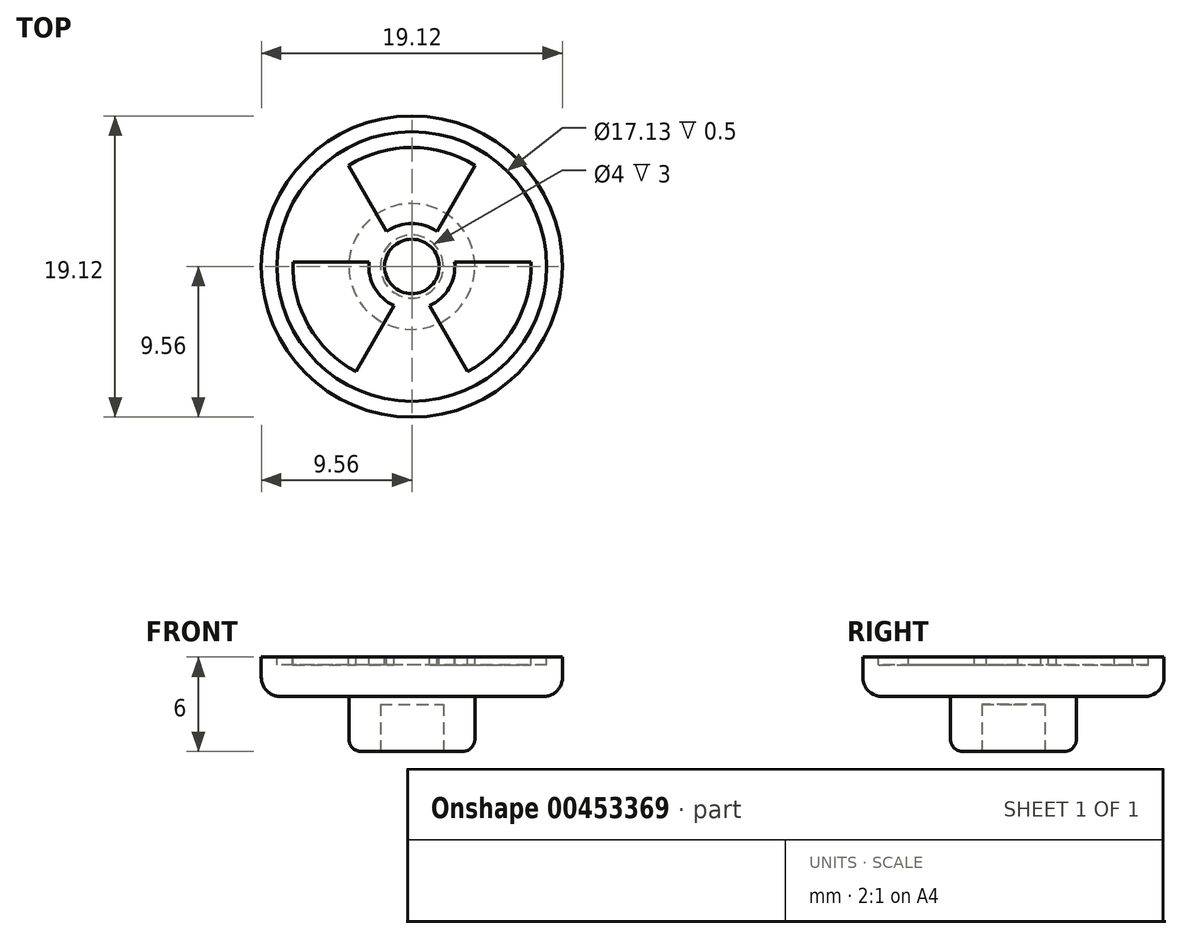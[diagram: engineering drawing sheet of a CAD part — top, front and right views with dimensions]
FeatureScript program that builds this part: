
annotation { "Feature Type Name" : "Feature", "Feature Type Description" : "" }
export const myFeature = defineFeature(function(context is Context, id is Id, definition is map)
    precondition{}
    {
        {
            var Q0;
            Q0=qCreatedBy(makeId("Top.planeOp"),FACE);
            var sketch = newSketch(context, id + "F0", { "sketchPlane" : qUnion([Q0])});
            skCircle(sketch, "E0", {"center": v(0, 0) * mm, "radius": 9.56 * mm});
            skSolve(sketch);
        }
        {
            var Q0;
            Q0=makeQuery(id+"F0.imprint","IMPRINT",FACE,{"disambiguationData":[TD([[makeQuery(id+"F0.imprint","IMPRINT",EDGE,{"derivedFrom":sQuery(id+"F0.wireOp",EDGE,"E0")}),1.0]])]});
            extrude(context, id + "F1", {"entities" : qUnion([Q0]), "depth" : 2.5 * mm, "offsetDistance" : 25 * mm});
        }
        {
            var Q0;
            Q0=makeQuery(id+"F1.opExtrude","CAP_FACE",FACE,{"disambiguationData":[OSD([sQuery(id+"F0.wireOp",EDGE,"E0")])],"isStart":false});
            var sketch = newSketch(context, id + "F2", { "sketchPlane" : qUnion([Q0])});
            skCircle(sketch, "E1", {"center": v(0, 0) * mm, "radius": 1.73 * mm});
            skArc(sketch, "E2", {"start": v(1.6, 2.22) * mm, "mid": v(0, 2.73) * mm, "end": v(-1.6, 2.22) * mm});
            skLineSegment(sketch, "E3", {"start": v(-1.6, 2.22) * mm, "end": v(-4.52, 7.28) * mm});
            skLineSegment(sketch, "E4", {"start": v(1.6, 2.22) * mm, "end": v(4.52, 7.28) * mm});
            skArc(sketch, "E5", {"start": v(4.52, 7.28) * mm, "mid": v(0, 8.56) * mm, "end": v(-4.52, 7.28) * mm});
            skLineSegment(sketch, "E6", {"start": v(0, 0) * mm, "end": v(8.28, 4.78) * mm, "construction": true});
            skLineSegment(sketch, "E7", {"start": v(0, 0) * mm, "end": v(-8.28, 4.78) * mm, "construction": true});
            skLineSegment(sketch, "E8", {"start": v(0, 0) * mm, "end": v(0, -15.72) * mm, "construction": true});
            skLineSegment(sketch, "E9.MirrorCS", {"start": v(2.72, 0.27) * mm, "end": v(8.56, 0.27) * mm});
            skArc(sketch, "E10.MirrorCS", {"start": v(2.72, 0.27) * mm, "mid": v(2.36, -1.36) * mm, "end": v(1.12, -2.49) * mm});
            skLineSegment(sketch, "E11.MirrorCS", {"start": v(1.12, -2.49) * mm, "end": v(4.04, -7.55) * mm});
            skArc(sketch, "E12.MirrorCS", {"start": v(8.56, 0.27) * mm, "mid": v(7.42, -4.28) * mm, "end": v(4.04, -7.55) * mm});
            skLineSegment(sketch, "E13.MirrorCS", {"start": v(-2.72, 0.27) * mm, "end": v(-8.56, 0.27) * mm});
            skArc(sketch, "E14.MirrorCS", {"start": v(-1.12, -2.49) * mm, "mid": v(-2.36, -1.36) * mm, "end": v(-2.72, 0.27) * mm});
            skLineSegment(sketch, "E15.MirrorCS", {"start": v(-1.12, -2.49) * mm, "end": v(-4.04, -7.55) * mm});
            skArc(sketch, "E16.MirrorCS", {"start": v(-4.04, -7.55) * mm, "mid": v(-7.42, -4.28) * mm, "end": v(-8.56, 0.27) * mm});
            skCircle(sketch, "E17", {"center": v(0, 0) * mm, "radius": 8.56 * mm});
            skCircle(sketch, "E18", {"center": v(0, 0) * mm, "radius": 7.56 * mm});
            skSolve(sketch);
        }
        {
            var Q0;
            Q0 = qSketchRegion(id + "F2", true);
            var Q1;
            Q1=makeQuery(id+"F2.imprint","IMPRINT",FACE,{"disambiguationData":[TD([[makeQuery(id+"F2.imprint","IMPRINT",EDGE,{"derivedFrom":sQuery(id+"F2.wireOp",EDGE,"E1")}),-1.0]])]});
            extrude(context, id + "F3", {"entities" : qUnion([Q0, Q1]), "operationType" : NewBodyOperationType.REMOVE, "oppositeDirection" : true, "depth" : .5 * mm, "offsetDistance" : 25 * mm});
        }
        {
            var Q0;
            Q0=makeQuery(id+"F1.opExtrude","CAP_FACE",FACE,{"disambiguationData":[OSD([sQuery(id+"F0.wireOp",EDGE,"E0")])],"isStart":true});
            var sketch = newSketch(context, id + "F4", { "sketchPlane" : qUnion([Q0])});
            skCircle(sketch, "E19", {"center": v(0, 0) * mm, "radius": 4 * mm});
            skSolve(sketch);
        }
        {
            var Q0;
            Q0=makeQuery(id+"F4.imprint","IMPRINT",FACE,{"disambiguationData":[TD([[makeQuery(id+"F4.imprint","IMPRINT",EDGE,{"derivedFrom":sQuery(id+"F4.wireOp",EDGE,"E19")}),1.0]])]});
            extrude(context, id + "F5", {"entities" : qUnion([Q0]), "operationType" : NewBodyOperationType.ADD, "depth" : 3.5 * mm, "offsetDistance" : 25 * mm});
        }
        {
            var Q0;
            Q0=makeQuery(id+"F1.opExtrude","CAP_EDGE",EDGE,{"disambiguationData":[OSD([sQuery(id+"F0.wireOp",EDGE,"E0")])],"isStart":true});
            fillet(context, id + "F6", {"entities" : qUnion([Q0]), "radius" : 1.2 * mm, "tangentPropagation" : true, "allowEdgeOverflow" : false});
        }
        {
            var Q0;
            Q0=makeQuery(id+"F5.opExtrude","CAP_FACE",FACE,{"disambiguationData":[OSD([sQuery(id+"F4.wireOp",EDGE,"E19")])],"isStart":false});
            var sketch = newSketch(context, id + "F7", { "sketchPlane" : qUnion([Q0])});
            skCircle(sketch, "E20", {"center": v(0, 0) * mm, "radius": 2 * mm});
            skSolve(sketch);
        }
        {
            var Q0;
            Q0=makeQuery(id+"F7.imprint","IMPRINT",FACE,{"disambiguationData":[TD([[makeQuery(id+"F7.imprint","IMPRINT",EDGE,{"derivedFrom":sQuery(id+"F7.wireOp",EDGE,"E20")}),1.0]])]});
            extrude(context, id + "F8", {"entities" : qUnion([Q0]), "operationType" : NewBodyOperationType.REMOVE, "oppositeDirection" : true, "depth" : 3 * mm, "offsetDistance" : 25 * mm});
        }
        {
            var Q0;
            Q0=makeQuery(id+"F5.opExtrude","CAP_EDGE",EDGE,{"disambiguationData":[OSD([sQuery(id+"F4.wireOp",EDGE,"E19")])],"isStart":false});
            fillet(context, id + "F9", {"entities" : qUnion([Q0]), "radius" : 0.8 * mm, "tangentPropagation" : true, "allowEdgeOverflow" : false});
        }
    });
